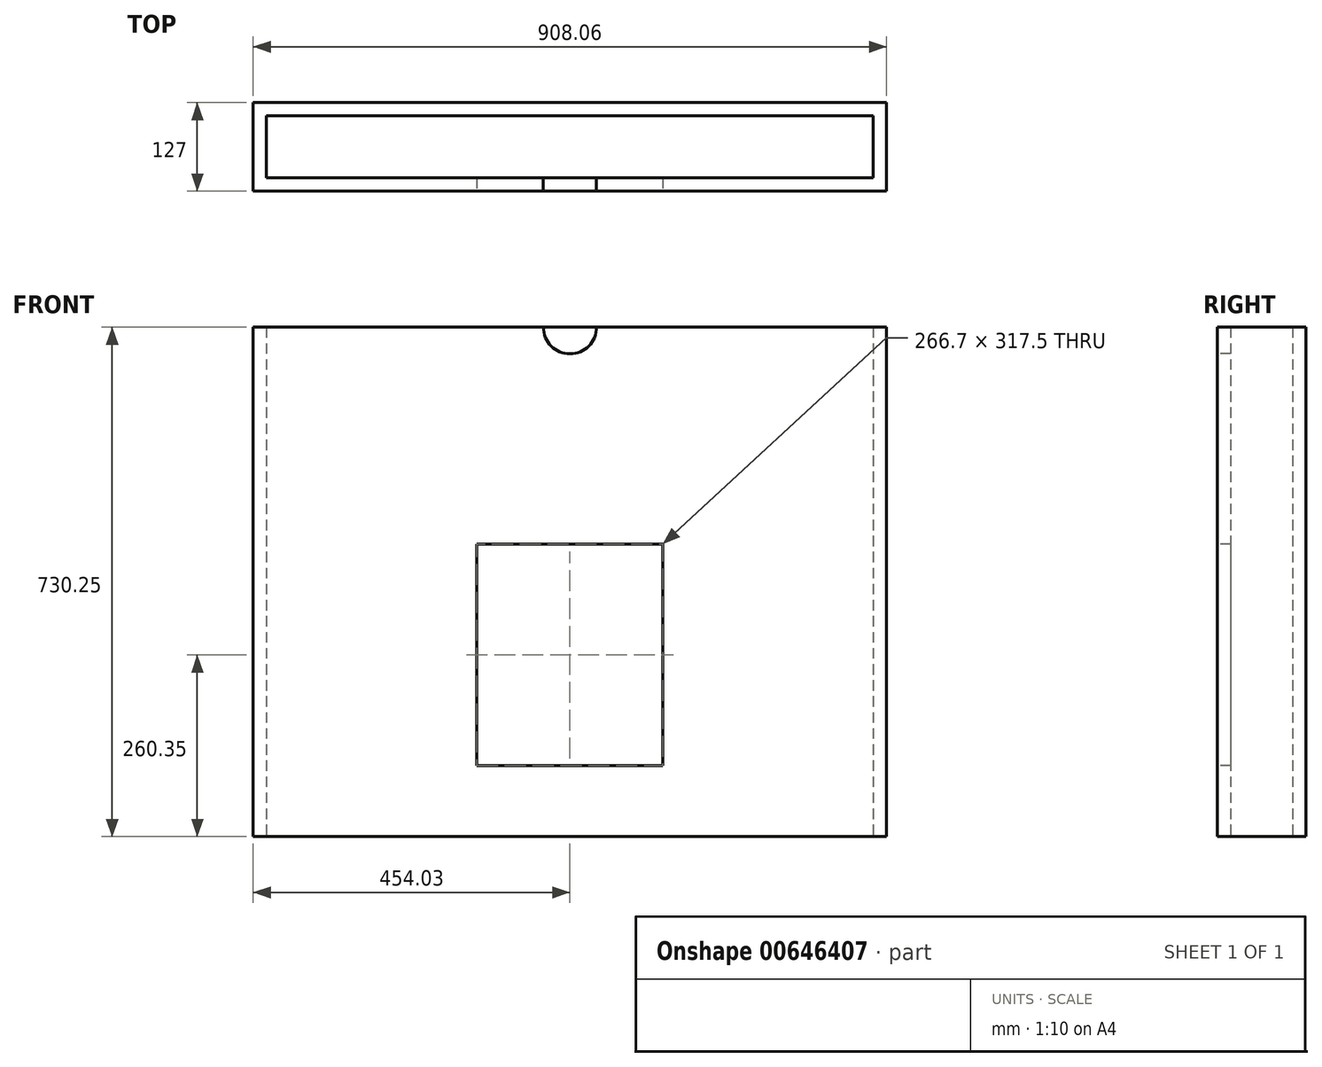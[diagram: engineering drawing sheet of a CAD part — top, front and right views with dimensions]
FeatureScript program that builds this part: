
annotation { "Feature Type Name" : "Feature", "Feature Type Description" : "" }
export const myFeature = defineFeature(function(context is Context, id is Id, definition is map)
    precondition{}
    {
        {
            var Q0;
            Q0=qCreatedBy(makeId("Top.planeOp"),FACE);
            var sketch = newSketch(context, id + "F0", { "sketchPlane" : qUnion([Q0])});
            skLineSegment(sketch, "E0.bottom", {"start": v(-454.03, 63.5) * mm, "end": v(454.03, 63.5) * mm});
            skLineSegment(sketch, "E0.top", {"start": v(-454.03, -63.5) * mm, "end": v(454.03, -63.5) * mm});
            skLineSegment(sketch, "E0.left", {"start": v(-454.03, 63.5) * mm, "end": v(-454.03, -63.5) * mm});
            skLineSegment(sketch, "E0.right", {"start": v(454.03, 63.5) * mm, "end": v(454.03, -63.5) * mm});
            skPoint(sketch, "E0.middle", {"position": v(0, 0) * mm});
            skLineSegment(sketch, "E1.bottom", {"start": v(-434.98, 44.45) * mm, "end": v(434.98, 44.45) * mm});
            skLineSegment(sketch, "E1.top", {"start": v(-434.98, -44.45) * mm, "end": v(434.98, -44.45) * mm});
            skLineSegment(sketch, "E1.left", {"start": v(-434.98, 44.45) * mm, "end": v(-434.98, -44.45) * mm});
            skLineSegment(sketch, "E1.right", {"start": v(434.98, 44.45) * mm, "end": v(434.98, -44.45) * mm});
            skSolve(sketch);
        }
        {
            var Q0;
            Q0=makeQuery(id+"F0.imprint","IMPRINT",FACE,{"disambiguationData":[TD([[makeQuery(id+"F0.imprint","IMPRINT",EDGE,{"derivedFrom":sQuery(id+"F0.wireOp",EDGE,"E0.bottom")}),-1.0]])]});
            extrude(context, id + "F1", {"entities" : qUnion([Q0]), "depth" : 730.25 * mm, "offsetDistance" : 25.4 * mm});
        }
        {
            var Q0;
            Q0=makeQuery(id+"F1.opExtrude","SWEPT_FACE",FACE,{"disambiguationData":[OSD([sQuery(id+"F0.wireOp",EDGE,"E0.top")])]});
            var sketch = newSketch(context, id + "F2", { "sketchPlane" : qUnion([Q0])});
            skLineSegment(sketch, "E2", {"start": v(0, 0) * mm, "end": v(0, 101.6) * mm});
            skLineSegment(sketch, "E3", {"start": v(0, 101.6) * mm, "end": v(0, 260.35) * mm});
            skLineSegment(sketch, "E4.bottom", {"start": v(133.35, 101.6) * mm, "end": v(-133.35, 101.6) * mm});
            skLineSegment(sketch, "E4.top", {"start": v(133.35, 419.1) * mm, "end": v(-133.35, 419.1) * mm});
            skLineSegment(sketch, "E4.left", {"start": v(133.35, 101.6) * mm, "end": v(133.35, 419.1) * mm});
            skLineSegment(sketch, "E4.right", {"start": v(-133.35, 101.6) * mm, "end": v(-133.35, 419.1) * mm});
            skPoint(sketch, "E4.middle", {"position": v(0, 260.35) * mm});
            skSolve(sketch);
        }
        {
            var Q0;
            Q0=makeQuery(id+"F2.imprint","IMPRINT",FACE,{"disambiguationData":[TD([[makeQuery(id+"F2.imprint","IMPRINT",EDGE,{"derivedFrom":sQuery(id+"F2.wireOp",EDGE,"E4.top")}),1.0]])]});
            extrude(context, id + "F3", {"entities" : qUnion([Q0]), "operationType" : NewBodyOperationType.REMOVE, "oppositeDirection" : true, "depth" : 25.4 * mm, "offsetDistance" : 25.4 * mm});
        }
        {
            var Q0;
            Q0=makeQuery(id+"F1.opExtrude","SWEPT_FACE",FACE,{"disambiguationData":[OSD([sQuery(id+"F0.wireOp",EDGE,"E0.top")])]});
            var sketch = newSketch(context, id + "F4", { "sketchPlane" : qUnion([Q0])});
            skLineSegment(sketch, "E5", {"start": v(0, 730.25) * mm, "end": v(0, 730.25) * mm});
            skPoint(sketch, "E5.endSnap0", {"position": v(0, 730.25) * mm});
            skCircle(sketch, "E6", {"center": v(0, 730.25) * mm, "radius": 38.1 * mm});
            skSolve(sketch);
        }
        {
            var Q0;
            Q0=makeQuery(id+"F4.imprint","IMPRINT",FACE,{"disambiguationData":[TD([[makeQuery(id+"F4.imprint","IMPRINT",EDGE,{"derivedFrom":sQuery(id+"F4.wireOp",EDGE,"E6")}),1.0]])]});
            extrude(context, id + "F5", {"entities" : qUnion([Q0]), "operationType" : NewBodyOperationType.REMOVE, "oppositeDirection" : true, "depth" : 25.4 * mm, "offsetDistance" : 25.4 * mm});
        }
    });
